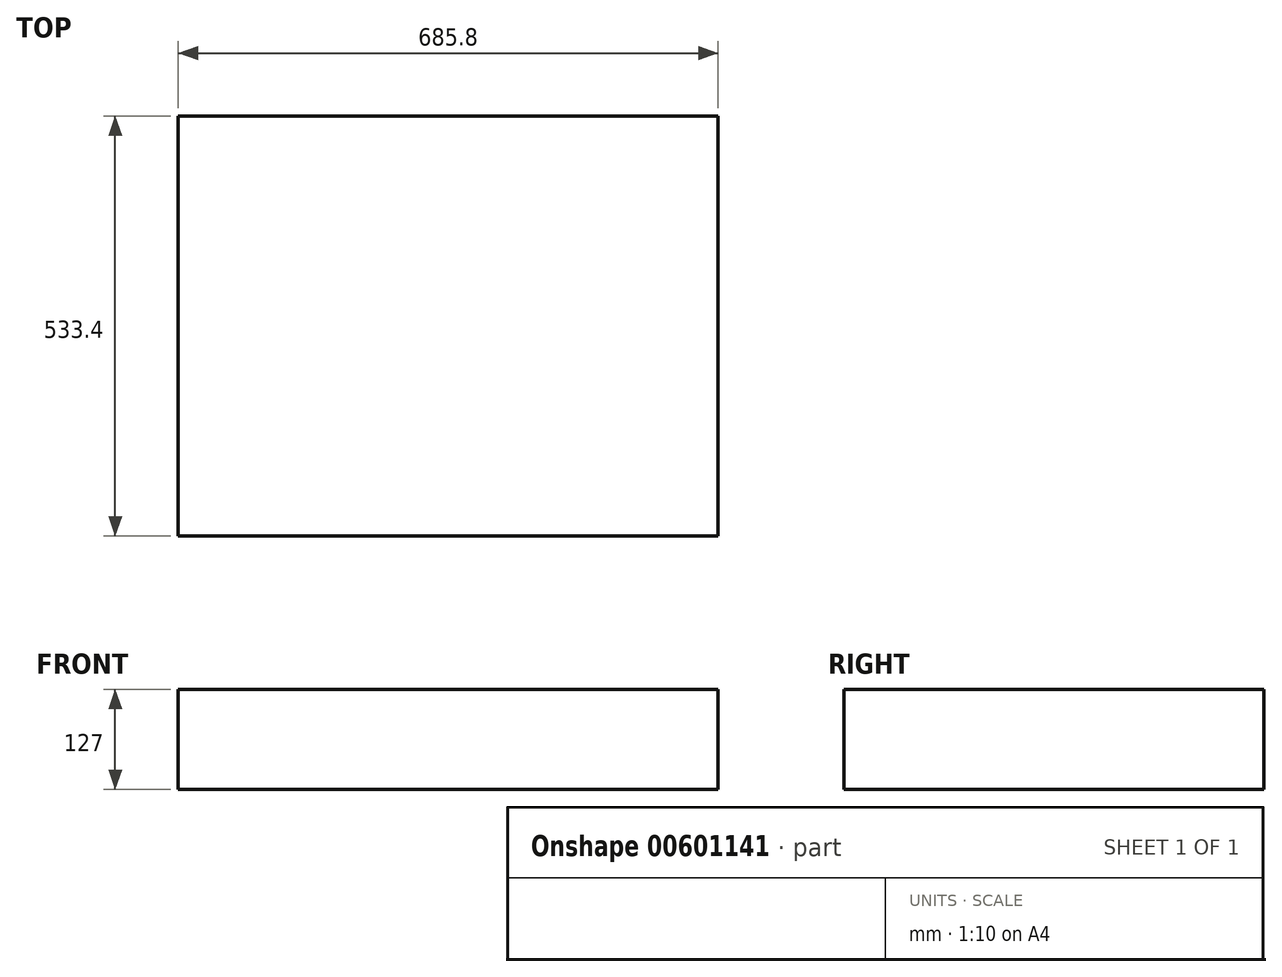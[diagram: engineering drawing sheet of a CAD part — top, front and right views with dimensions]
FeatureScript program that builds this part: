
annotation { "Feature Type Name" : "Feature", "Feature Type Description" : "" }
export const myFeature = defineFeature(function(context is Context, id is Id, definition is map)
    precondition{}
    {
        {
            var Q0;
            Q0=qCreatedBy(makeId("Top.planeOp"),FACE);
            var sketch = newSketch(context, id + "F0", { "sketchPlane" : qUnion([Q0])});
            skLineSegment(sketch, "E0.bottom", {"start": v(342.9, 266.7) * mm, "end": v(-342.9, 266.7) * mm});
            skLineSegment(sketch, "E0.top", {"start": v(342.9, -266.7) * mm, "end": v(-342.9, -266.7) * mm});
            skLineSegment(sketch, "E0.left", {"start": v(342.9, 266.7) * mm, "end": v(342.9, -266.7) * mm});
            skLineSegment(sketch, "E0.right", {"start": v(-342.9, 266.7) * mm, "end": v(-342.9, -266.7) * mm});
            skPoint(sketch, "E0.middle", {"position": v(0, 0) * mm});
            skSolve(sketch);
        }
        {
            var Q0;
            Q0 = qSketchRegion(id + "F0", true);
            extrude(context, id + "F1", {"entities" : qUnion([Q0]), "depth" : 127 * mm, "offsetDistance" : 25.4 * mm});
        }
    });
